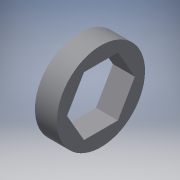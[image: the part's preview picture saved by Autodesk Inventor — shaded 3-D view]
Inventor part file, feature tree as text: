
AUTODESK INVENTOR PART (.ipt)
format: ipt  version: 2018 (Build 220112000, 112)  size: 103,936 bytes
history: native  units: in
note: dims shown in document units (in); Inventor stores cm internally (conversion verified against a paired STEP export)
features: extrude x1, sketch x1
ambient origin geometry x8: Origin, YZ Plane, XZ Plane, XY Plane, X Axis, Y Axis, Z Axis, Center Point
bodies: Solid1 (feature_tree)
feature tree (2):
  extrude  "Extrusion1"  Depth=0.186in TaperAngle=0.0deg
  sketch  "Sketch1"  dims[d0=0.75in d3=0.186in d4=0.0in]
